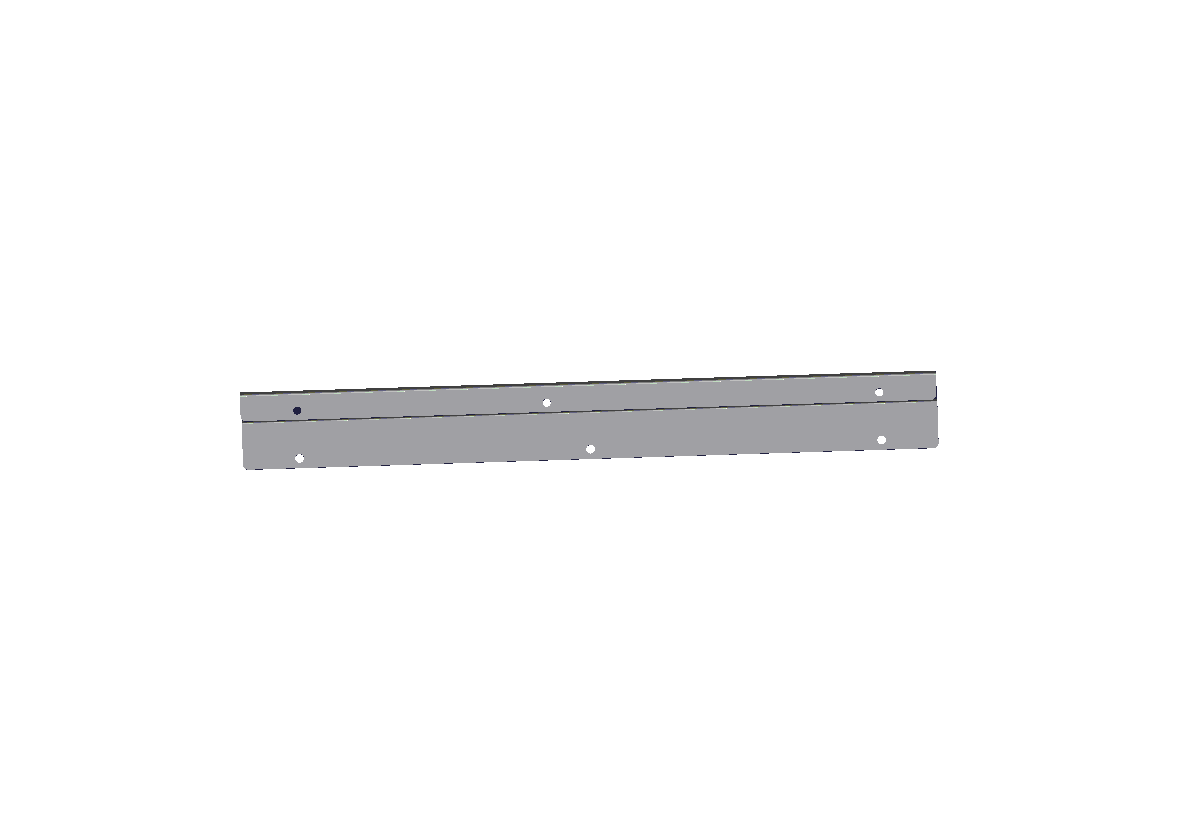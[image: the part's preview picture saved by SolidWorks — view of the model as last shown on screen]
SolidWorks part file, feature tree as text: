
SOLIDWORKS PART (.sldprt)
format: sldprt  version: not decoded by parser v0  size: 1,083,904 bytes
history: native  units: mm
features: sketch x11, cut_extrude x7, sheet_metal_op x3, pattern_linear x3, material x1, fillet x1, plane x1 + 3 further entries (+13 scaffold rows collapsed)
feature tree (43):
  scaffold x13  (default folders/planes/origin — collapsed)
  material  "Material <not specified>"
  "Design Table"
  sketch  "Sketch1"  dims[D1=~153.723053mm Width=424.942mm Back Panel Height=123.3424mm]
  sheet_metal_op  "Sheet-Metal1"  Thickness=1.2192mm
  sheet_metal_op  "Base-Flange"
  sketch  "Sketch9"  dims[c1.D1=1.778mm c1.D4=90.0deg c1.D5=1.0 c1.D8=0.1mm c1.D9=0.1mm c2.D1=1.778mm c2.D6=10.0mm c2.Edge-Flange2=0.0]
  sketch  "Sketch12"
  sheet_metal_op  "EdgeBend2"
  sketch  "Sketch13"  dims[c1.D1=4.953mm c1.D2=5.4102mm c1.D3=5.4102mm c1.D4=5.4102mm c1.D6=4.318mm c2.D2=12.7mm c2.D3=12.7mm c2.D4=139.7mm c2.D5=34.2265mm c2.D6=35.4965mm c3.D5=~34.66465mm c3.D3=215.9mm]
  cut_extrude  "8-32 Clearance For Chassi Studs"  [1 undecoded]
  sketch  "Sketch14"  dims[c1.D1=5.4102mm c1.D2=5.4102mm c1.D4=5.4102mm c1.D5=5.4102mm c2.D2=34.8742mm c2.D3=6.35mm c2.D4=177.8mm c2.D5=6.35mm c3.D3=25.4mm c3.D5=34.4678mm c3.D2=34.671mm c4.D5=34.4678mm c4.D2=212.471mm]
  cut_extrude  "8-32 PEM Nuts For Cover Attachment"  [1 undecoded]
  fillet  "Fillet1"  Radius=3.175mm
  sketch  "Sketch16"  dims[c1.D1=4.7625mm c1.D2=3.556mm c1.D4=3.556mm c2.D2=32.512mm c2.D3=9.525mm c2.D4=79.375mm c2.D5=15.24mm c2.D6=7.62mm c2.D7=6.35mm c3.D3=6.35mm c3.D7=30.48mm]
  cut_extrude  "Cut-Extrude5"  Depth=12.54mm
  pattern_linear  "LPattern1"  Count1=16 Count2=1 Spacing1=19.05mm Spacing2=50mm
  sketch  "Sketch17"  dims[D1=180.34mm D2=3.556mm D3=17.78mm D4=13.97mm]
  cut_extrude  "NIC port"  Depth=2.54mm
  sketch  "air holes"  dims[c1.D1=3.556mm c1.D2=5.08mm c1.D5=3.556mm c1.D3=~10.675636mm c2.D2=8.89mm c2.D3=25.4mm c2.D4=197.5358mm]
  cut_extrude  "Cut-Extrude7"  Depth=2.54mm
  pattern_linear  "air hole pattern"  Count1=3 Count2=40 Spacing1=5.08mm Spacing2=7.62mm
  sketch  "fan mount holes"  dims[c1.D1=1.778mm c1.D2=3.556mm c1.D3=3.556mm c1.D4=3.556mm c1.D5=3.556mm c1.D12=32.0mm c1.D6=16.0mm c1.D7=16.0mm c1.D8=16.0mm c1.D9=16.0mm c1.D10=71.12mm c1.D11=50.8mm c2.D1=16.0mm c2.D6=16.0mm c2.D7=16.0mm c2.D8=16.0mm c2.D9=19.05mm c2.D10=60.96mm]
  cut_extrude  "Cut-Extrude9"  Depth=2.54mm
  pattern_linear  "LPattern2"  Count1=2 Count2=1 Spacing1=50.8mm Spacing2=63.5mm
  plane  "Plane1"
  sketch  "Sketch18"  dims[D1=8.382mm D2=38.1mm D3=25.4mm]
  cut_extrude  "Hole for Power Jack"  Depth=2.54mm
  "Flat-Pattern1"
  sketch  "Bend-Lines1"
  "Flatten-<EdgeBend2>1"
decode coverage: 19 of 25 modeling features carry decoded parameters; 3 rows unclassified (native names shown)
note: ~ marks probable driven/reference dimensions
note: 2 parameter values undecoded
note: suppression state not decoded; provenance and decode notes live in map.json
